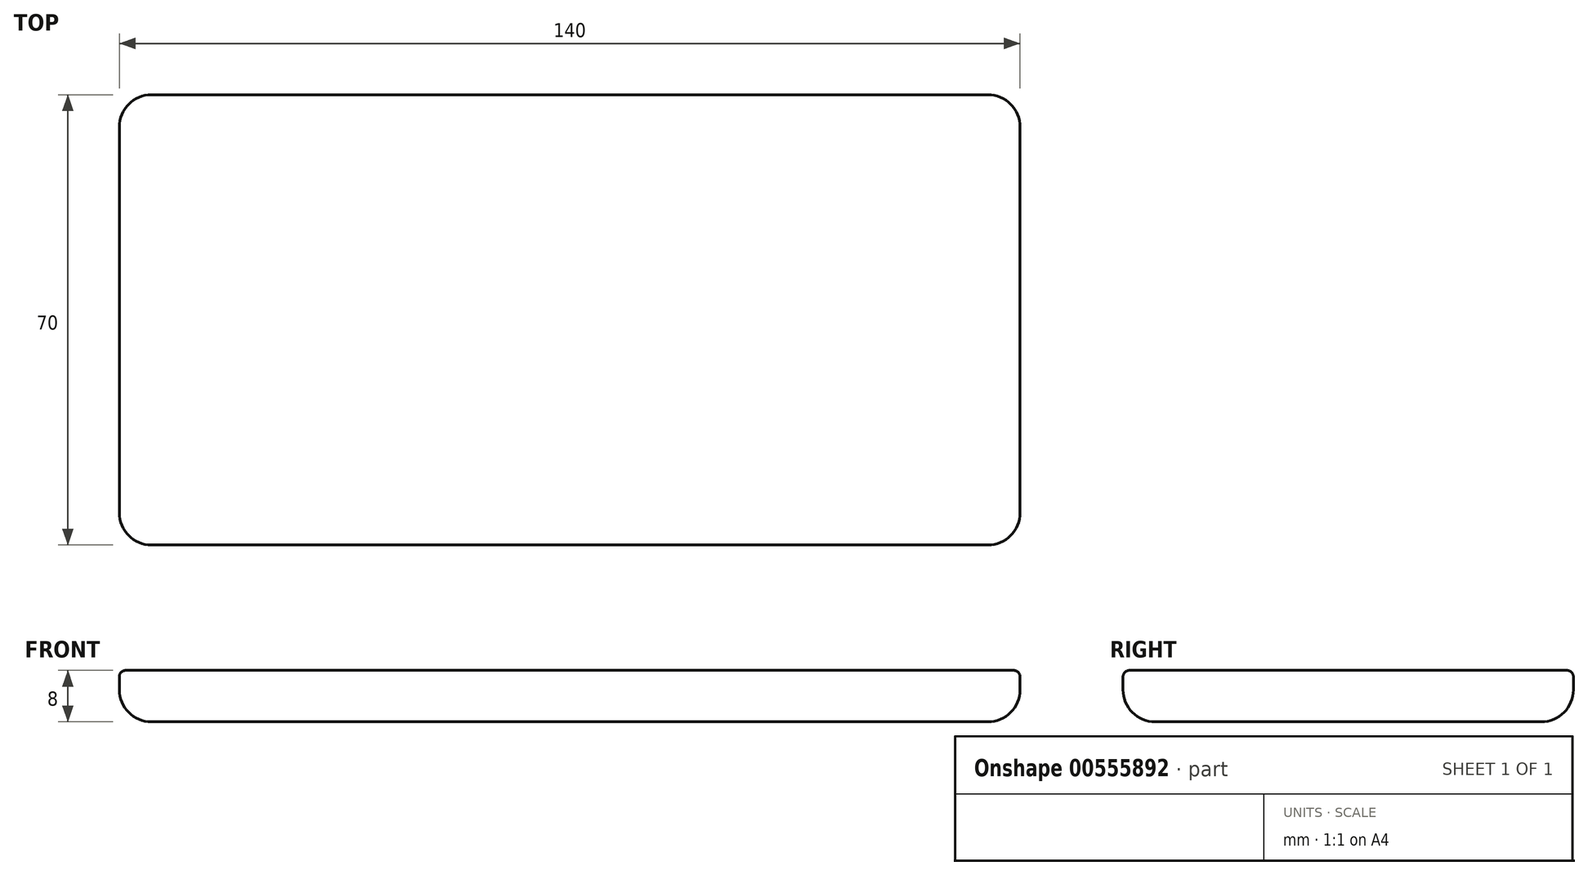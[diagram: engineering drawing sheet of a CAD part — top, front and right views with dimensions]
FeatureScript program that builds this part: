
annotation { "Feature Type Name" : "Feature", "Feature Type Description" : "" }
export const myFeature = defineFeature(function(context is Context, id is Id, definition is map)
    precondition{}
    {
        {
            var Q0;
            Q0=qCreatedBy(makeId("Top.planeOp"),FACE);
            var sketch = newSketch(context, id + "F0", { "sketchPlane" : qUnion([Q0])});
            skLineSegment(sketch, "E0.bottom", {"start": v(-61.24, 46.97) * mm, "end": v(68.76, 46.97) * mm});
            skLineSegment(sketch, "E0.top", {"start": v(-61.24, -23.03) * mm, "end": v(68.76, -23.03) * mm});
            skLineSegment(sketch, "E0.left", {"start": v(-66.24, 41.97) * mm, "end": v(-66.24, -18.03) * mm});
            skLineSegment(sketch, "E0.right", {"start": v(73.76, 41.97) * mm, "end": v(73.76, -18.03) * mm});
            skPoint(sketch, "E1.visualSharp", {"position": v(-66.24, 46.97) * mm});
            skArc(sketch, "E1.filletArc", {"start": v(-61.24, 46.97) * mm, "mid": v(-64.78, 45.5) * mm, "end": v(-66.24, 41.97) * mm});
            skPoint(sketch, "E2.visualSharp", {"position": v(-66.24, -23.03) * mm});
            skArc(sketch, "E2.filletArc", {"start": v(-66.24, -18.03) * mm, "mid": v(-64.78, -21.57) * mm, "end": v(-61.24, -23.03) * mm});
            skPoint(sketch, "E3.visualSharp", {"position": v(73.76, -23.03) * mm});
            skArc(sketch, "E3.filletArc", {"start": v(68.76, -23.03) * mm, "mid": v(72.3, -21.57) * mm, "end": v(73.76, -18.03) * mm});
            skPoint(sketch, "E4.visualSharp", {"position": v(73.76, 46.97) * mm});
            skArc(sketch, "E4.filletArc", {"start": v(73.76, 41.97) * mm, "mid": v(72.3, 45.5) * mm, "end": v(68.76, 46.97) * mm});
            skSolve(sketch);
        }
        {
            var Q0;
            Q0 = qSketchRegion(id + "F0", true);
            extrude(context, id + "F1", {"entities" : qUnion([Q0]), "depth" : 8 * mm, "offsetDistance" : 25 * mm});
        }
        {
            var Q0;
            Q0=makeQuery(id+"F1.opExtrude","CAP_EDGE",EDGE,{"disambiguationData":[OSD([sQuery(id+"F0.wireOp",EDGE,"E0.top")])],"isStart":true});
            var Q1;
            Q1=makeQuery(id+"F1.opExtrude","CAP_EDGE",EDGE,{"disambiguationData":[OSD([sQuery(id+"F0.wireOp",EDGE,"E0.right")])],"isStart":true});
            fillet(context, id + "F2", {"entities" : qUnion([Q0, Q1]), "radius" : 5 * mm, "tangentPropagation" : true, "allowEdgeOverflow" : false});
        }
        {
            var Q0;
            Q0=makeQuery(id+"F1.opExtrude","CAP_FACE",FACE,{"disambiguationData":[OSD([sQuery(id+"F0.wireOp",EDGE,"E0.bottom"),sQuery(id+"F0.wireOp",EDGE,"E0.top"),sQuery(id+"F0.wireOp",EDGE,"E0.left"),sQuery(id+"F0.wireOp",EDGE,"E0.right"),sQuery(id+"F0.wireOp",EDGE,"E1.filletArc"),sQuery(id+"F0.wireOp",EDGE,"E2.filletArc"),sQuery(id+"F0.wireOp",EDGE,"E3.filletArc"),sQuery(id+"F0.wireOp",EDGE,"E4.filletArc")])],"isStart":false});
            fillet(context, id + "F3", {"entities" : qUnion([Q0]), "radius" : 1 * mm, "tangentPropagation" : true, "allowEdgeOverflow" : false});
        }
    });
